# Revit family: 2079000(n0300)
name_source: partatom
category: Security Devices
units: mm (PartAtom-declared; Revit-internal decimal feet)

## family parameters
Always vertical = No
Cut with Voids When Loaded = No
Host = Ceiling
OmniClass Number = 23.85.30.14
OmniClass Title = Presence Detection/Registration
Room Calculation Point = No
Shared = Yes

## types (2) — shared parameters
zero-valued in all types: A

## per-type parameters (varying)
- Type 1: CTN=0; EF000218=0 mm  [stored 0 ft]; EF000846=0 mm  [stored 0 ft]; EF001322=0 mm  [stored 0 ft]; EF001323=0 mm  [stored 0 ft]; EF003843=0 mm  [stored 0 ft]; EF003882=0; EF004265=0 mm  [stored 0 ft]; EF006589=0; EF006590=0; EF008011=0 mm  [stored 0 ft]; EF010517=0 mm  [stored 0 ft]; EF010886=0 mm  [stored 0 ft]; EF010945=0 mm  [stored 0 ft]; EF010946=0 mm  [stored 0 ft]; LOG=0; NOCUPEROU=0; PRICEQUANTITY=0; QUANTITYINT=0; QUANTITYMIN=0
- 2079000: ARTICLENO=NB; BOMINFO=LINA; CATALOG=Theben; COO=HU; CTN=90314990; DEEPLINK_PRODUKTSEITE=http://www.theben.de; DESCLONG=KNX presence detector for ceiling mounting, Three channels light for control of three light groups, Switching or constant light control, Operation as full or semi-automatic switchable, Brightness channel with cyclic output, Channel for room monitoring, Shortening of overrun time light at short presence, Mixed light measurement, Extended square detection area, Light off delay self-learning, Switching between 2 brightness setpoints, Brightness setpoints adjustable via bus, Stand-by functionality, 2 presence channels with switch-on delay/inactive, Switch-off delay adjustable, Parameters can be remotely controlled and read out (SendoPro 868-A), Master/slave operation selectable, Test functions, Scene control with two scenes, 8-bit scenes, Integrated bus coupling unit; DESCSHORT=KNX presence detector for ceiling mounting, 3xlight and 2xHVAC, max. 10x10 m; EF000003=EV000383; EF000007=White; EF000010=Presence detector; EF000139=Untreated; EF000147=false; EF000218=16 mm  [stored 0.0524934 ft]; EF000846=29 mm  [stored 0.0951444 ft]; EF001098=true; EF001257=Thermoplast; EF001322=5000 mm; EF001323=5000 mm; EF002169=Plastic; EF003843=10000 mm; EF003876=true; EF003882=9010; EF003898=true; EF004265=29 mm  [stored 0.0951444 ft]; EF006243=false; EF006311=false; EF006569=matt; EF006582=0, 360 °; EF006589=30; EF006590=60; EF007575=true; EF008011=3000 mm; EF010517=42 mm  [stored 0.137795 ft]; EF010886=20 mm  [stored 0.0656168 ft]; EF010945=110 mm  [stored 0.360892 ft]; EF010946=65 mm  [stored 0.213255 ft]; GEBRAUCHSANLEITUNG=http://www.theben.de; INTNO=7612748004450; LINA=2079000; LOG=300; MANUID=2079000; MANUNAME=Theben AG; MANUTYPEDESC=thePrema P360 KNX UP WH; Manufacturer=Theben; Model=2079000; NB=2079000(N0300); NBSYN=$MANUID.($SA.$A.$LOG.); NN=thePrema P KNX; NOCUPEROU=1; PRICEQUANTITY=1; PRODUKTDATENBLATT=http://www.theben.de; QUANTITYINT=1; QUANTITYMIN=1; REACH_ERKLAERUNG=http://www.theben.de; REMARKS=ERP-GROUP 360; SA=None; SUPPLIER=THEBEN; SUPPLIERALTNO=2079000

note: [stored X ft] marks values corroborated as IEEE doubles in the binary element streams (Revit-internal decimal feet)

## geometry (parser evidence)
native form markers: Sweep x11
no freeform markers — native parametric forms only
